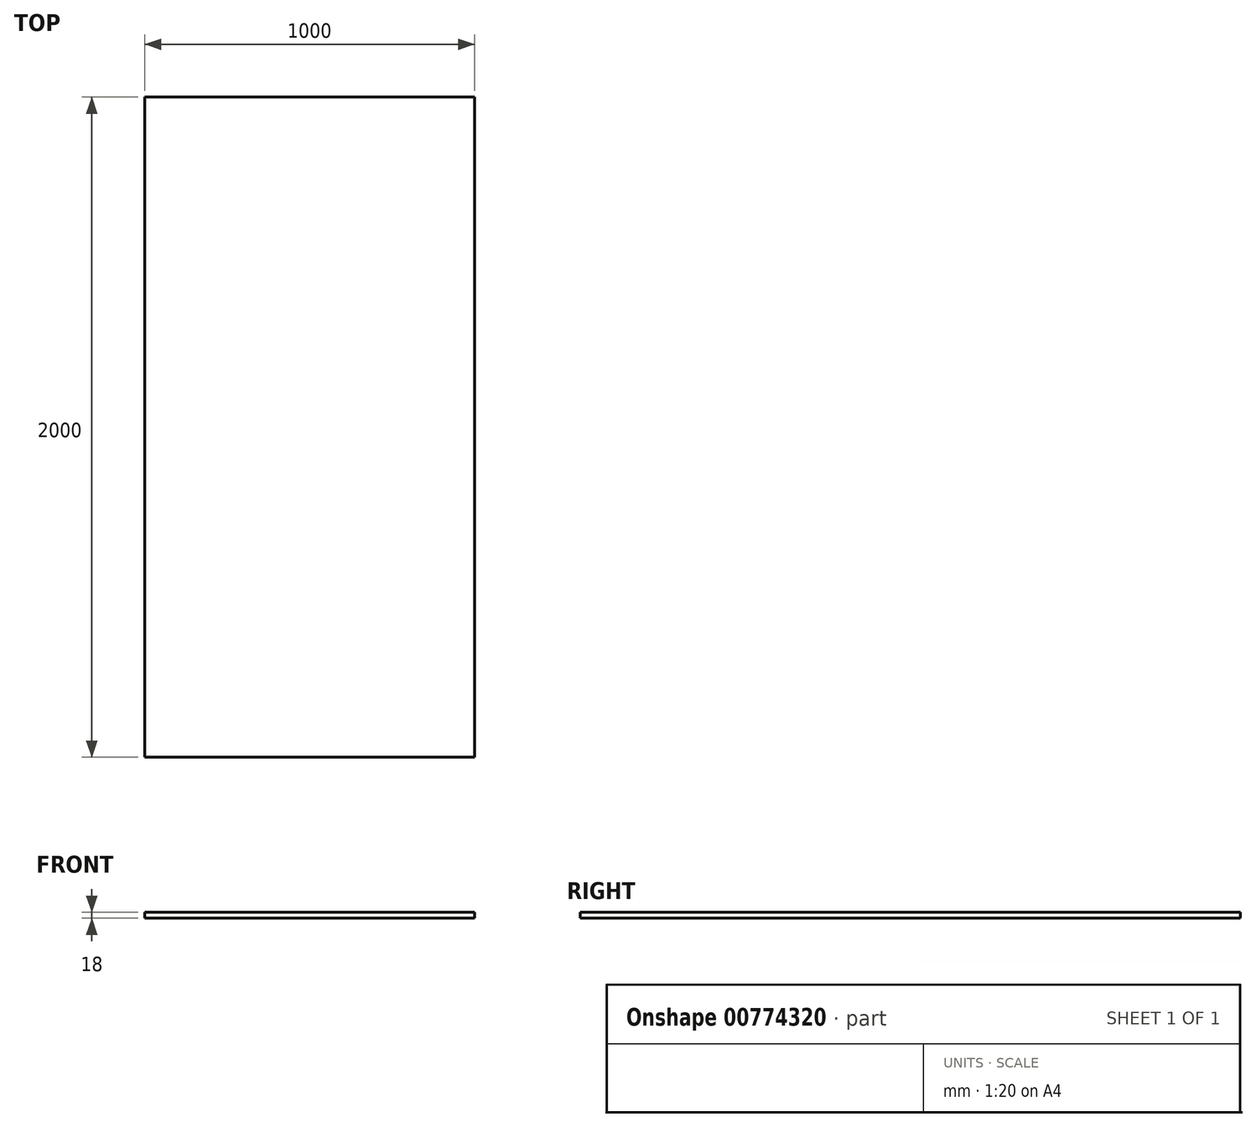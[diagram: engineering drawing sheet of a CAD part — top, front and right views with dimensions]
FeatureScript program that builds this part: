
annotation { "Feature Type Name" : "Feature", "Feature Type Description" : "" }
export const myFeature = defineFeature(function(context is Context, id is Id, definition is map)
    precondition{}
    {
        {
            var Q0;
            Q0=qCreatedBy(makeId("Top.planeOp"),FACE);
            var sketch = newSketch(context, id + "F0", { "sketchPlane" : qUnion([Q0])});
            skLineSegment(sketch, "E0.bottom", {"start": v(500, 1000) * mm, "end": v(-500, 1000) * mm});
            skLineSegment(sketch, "E0.top", {"start": v(500, -1000) * mm, "end": v(-500, -1000) * mm});
            skLineSegment(sketch, "E0.right", {"start": v(-500, 1000) * mm, "end": v(-500, -1000) * mm});
            skPoint(sketch, "E0.middle", {"position": v(0, 0) * mm});
            skLineSegment(sketch, "E1", {"start": v(500, 1000) * mm, "end": v(500, -1000) * mm});
            skSolve(sketch);
        }
        {
            var Q0;
            Q0=makeQuery(id+"F0.imprint","IMPRINT",FACE,{"disambiguationData":[TD([[makeQuery(id+"F0.imprint","IMPRINT",EDGE,{"derivedFrom":sQuery(id+"F0.wireOp",EDGE,"E0.bottom")}),1.0]])]});
            extrude(context, id + "F1", {"entities" : qUnion([Q0]), "depth" : 18 * mm, "offsetDistance" : 25 * mm});
        }
    });
